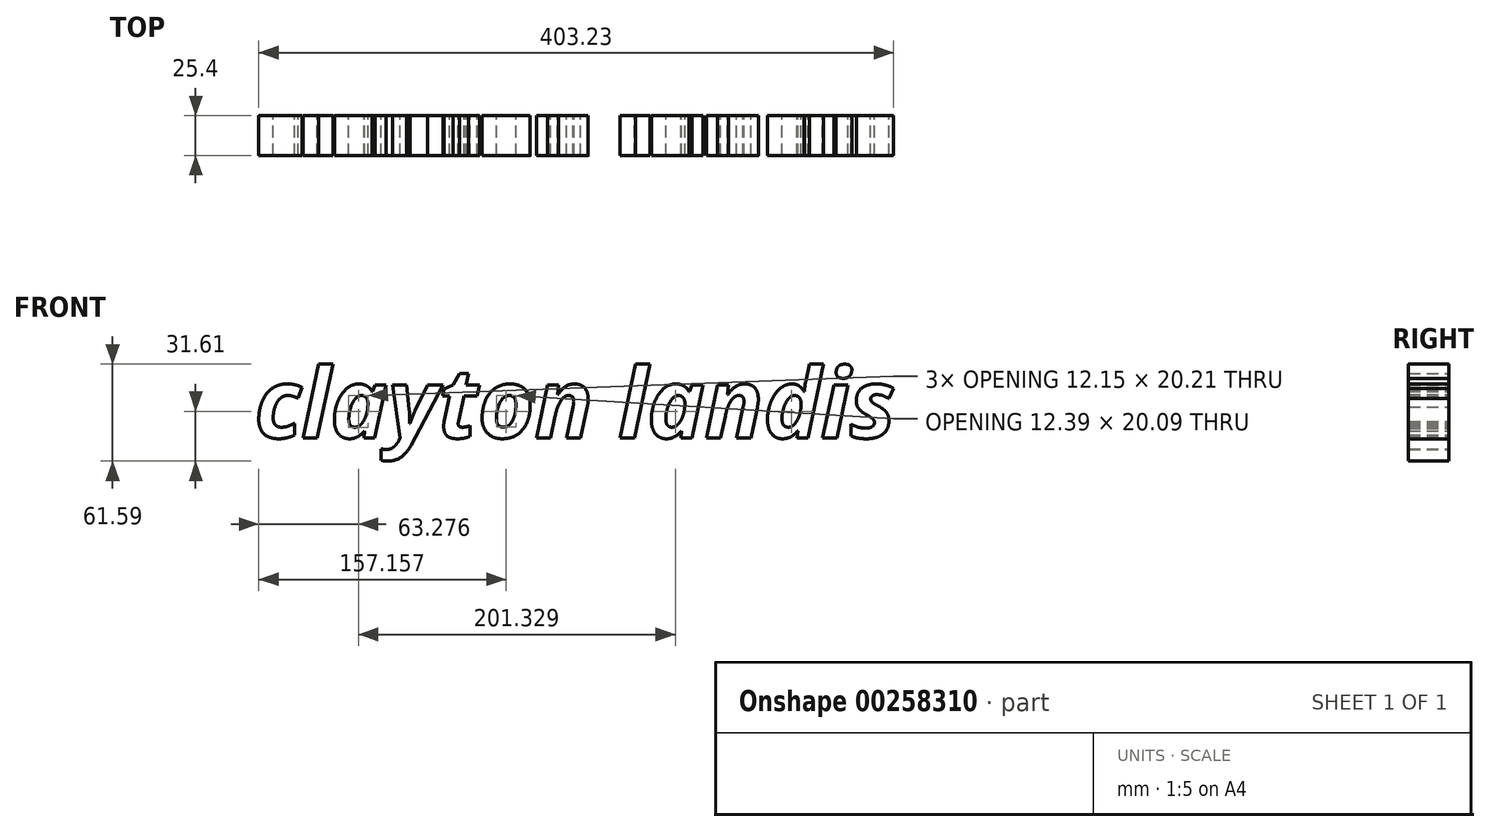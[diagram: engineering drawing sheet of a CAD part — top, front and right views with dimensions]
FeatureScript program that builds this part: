
annotation { "Feature Type Name" : "Feature", "Feature Type Description" : "" }
export const myFeature = defineFeature(function(context is Context, id is Id, definition is map)
    precondition{}
    {
        {
            var Q0;
            Q0=qCreatedBy(makeId("Front.planeOp"),FACE);
            var sketch = newSketch(context, id + "F0", { "sketchPlane" : qUnion([Q0])});
            skText(sketch, "E0", { "text": "clayton landis", "fontName": "OpenSans-BoldItalic.ttf"});
            const initialGuessF0  = {"E0": [-0.21362, 0, 1, 0, 0.04434]};
            skSetInitialGuess(sketch, initialGuessF0);
            skSolve(sketch);
        }
        {
            var Q0;
            Q0 = qSketchRegion(id + "F0", true);
            extrude(context, id + "F1", {"entities" : qUnion([Q0]), "depth" : 25.4 * mm});
        }
    });
